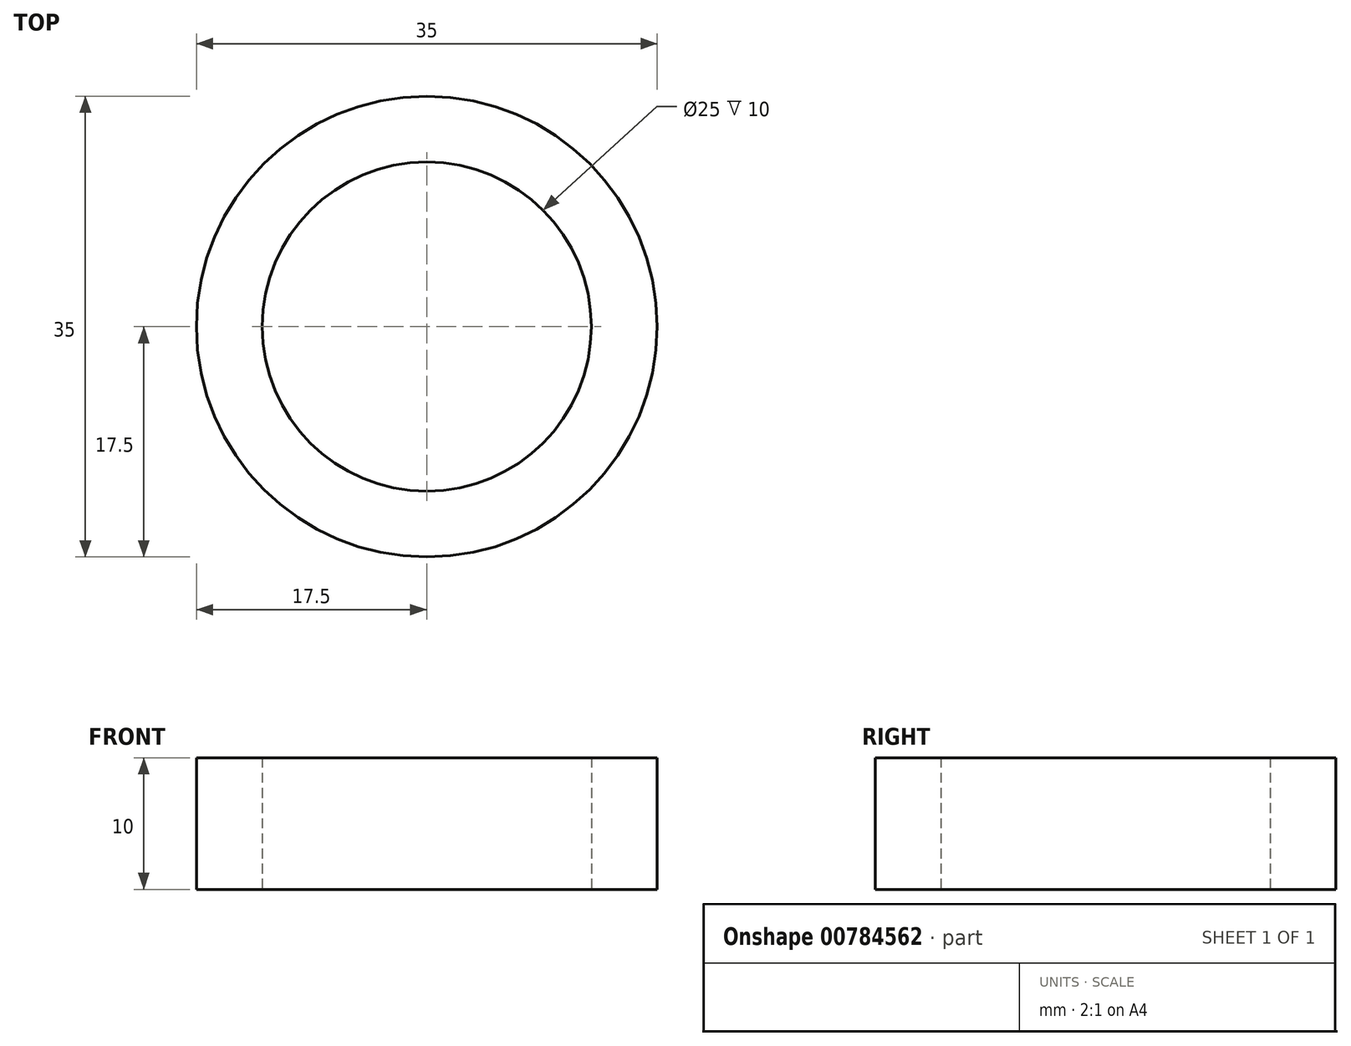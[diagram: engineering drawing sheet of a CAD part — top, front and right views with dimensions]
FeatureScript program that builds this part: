
annotation { "Feature Type Name" : "Feature", "Feature Type Description" : "" }
export const myFeature = defineFeature(function(context is Context, id is Id, definition is map)
    precondition{}
    {
        {
            var Q0;
            Q0=qCreatedBy(makeId("Top.planeOp"),FACE);
            var sketch = newSketch(context, id + "F0", { "sketchPlane" : qUnion([Q0])});
            skCircle(sketch, "E0", {"center": v(0, 0) * mm, "radius": 12.5 * mm});
            skCircle(sketch, "E1", {"center": v(0, 0) * mm, "radius": 17.5 * mm});
            skSolve(sketch);
        }
        {
            var Q0;
            Q0=makeQuery(id+"F0.imprint","IMPRINT",FACE,{"disambiguationData":[TD([[makeQuery(id+"F0.imprint","IMPRINT",EDGE,{"derivedFrom":sQuery(id+"F0.wireOp",EDGE,"E0")}),-1.0]])]});
            extrude(context, id + "F1", {"entities" : qUnion([Q0]), "depth" : 10 * mm, "offsetDistance" : 25 * mm});
        }
    });
